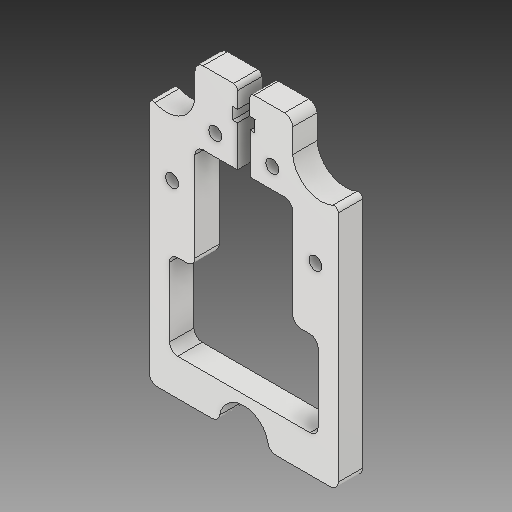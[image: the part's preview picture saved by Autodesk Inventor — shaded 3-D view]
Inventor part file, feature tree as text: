
AUTODESK INVENTOR PART (.ipt)
format: ipt  version: 2018 (Build 220112000, 112)  size: 204,288 bytes
history: native  units: mm
features: other x3, sketch x2
ambient origin geometry x8: Origin, YZ Plane, XZ Plane, XY Plane, X Axis, Y Axis, Z Axis, Center Point
bodies: Solid1 (feature_tree)
feature tree (5):
  other  "Hotend Slide Part 2_MIR.ipt"
  other  "Solid1::Hotend Slide Part 2_MIR.ipt"
  other  "TaggingFeature1"
  sketch  "Sketch1"  dims[d0=10.0mm]
  sketch  "Sketch2"
